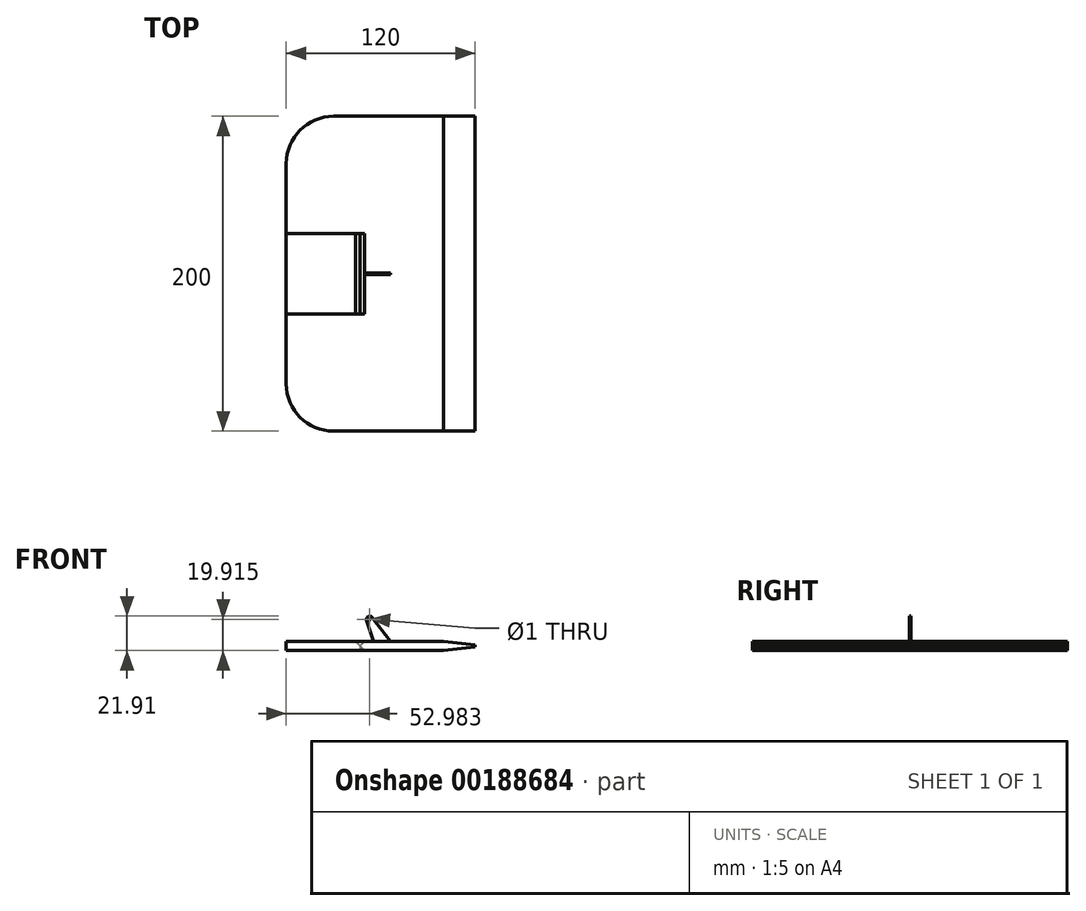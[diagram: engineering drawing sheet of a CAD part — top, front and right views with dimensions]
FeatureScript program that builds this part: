
annotation { "Feature Type Name" : "Feature", "Feature Type Description" : "" }
export const myFeature = defineFeature(function(context is Context, id is Id, definition is map)
    precondition{}
    {
        {
            var Q0;
            Q0=qCreatedBy(makeId("Top.planeOp"),FACE);
            var sketch = newSketch(context, id + "F0", { "sketchPlane" : qUnion([Q0])});
            skLineSegment(sketch, "E0.bottom", {"start": v(61.57, 100) * mm, "end": v(-28.43, 100) * mm});
            skLineSegment(sketch, "E0.top", {"start": v(61.57, -100) * mm, "end": v(-28.43, -100) * mm});
            skLineSegment(sketch, "E0.left", {"start": v(61.57, 100) * mm, "end": v(61.57, -100) * mm});
            skLineSegment(sketch, "E0.right", {"start": v(-58.43, 70) * mm, "end": v(-58.43, -70) * mm});
            skPoint(sketch, "E0.middle", {"position": v(1.57, 0) * mm});
            skPoint(sketch, "E1.visualSharp", {"position": v(-58.43, -100) * mm});
            skArc(sketch, "E1.filletArc", {"start": v(-58.43, -70) * mm, "mid": v(-49.64, -91.21) * mm, "end": v(-28.43, -100) * mm});
            skPoint(sketch, "E2.visualSharp", {"position": v(-58.43, 100) * mm});
            skArc(sketch, "E2.filletArc", {"start": v(-28.43, 100) * mm, "mid": v(-49.64, 91.21) * mm, "end": v(-58.43, 70) * mm});
            skLineSegment(sketch, "E3.bottom", {"start": v(-58.43, -25.5) * mm, "end": v(-11.6, -25.5) * mm});
            skLineSegment(sketch, "E3.left", {"start": v(-58.43, -25.5) * mm, "end": v(-58.43, 0) * mm});
            skLineSegment(sketch, "E3.right", {"start": v(-11.6, -25.5) * mm, "end": v(-11.6, 0) * mm});
            skLineSegment(sketch, "E4.MirrorCS", {"start": v(-58.43, 25.5) * mm, "end": v(-11.6, 25.5) * mm});
            skLineSegment(sketch, "E5.MirrorCS", {"start": v(-11.6, 25.5) * mm, "end": v(-11.6, 0) * mm});
            skLineSegment(sketch, "E6.MirrorCS", {"start": v(-58.43, 25.5) * mm, "end": v(-58.43, 0) * mm});
            skSolve(sketch);
        }
        {
            var Q0;
            Q0=makeQuery(id+"F0.imprint","IMPRINT",FACE,{"disambiguationData":[TD([[makeQuery(id+"F0.imprint","IMPRINT",EDGE,{"derivedFrom":sQuery(id+"F0.wireOp",EDGE,"E0.bottom")}),1.0]])]});
            extrude(context, id + "F1", {"entities" : qUnion([Q0]), "depth" : 6 * mm});
        }
        {
            var Q0;
            Q0=makeQuery(id+"F1.opExtrude","CAP_EDGE",EDGE,{"disambiguationData":[OSD([sQuery(id+"F0.wireOp",EDGE,"E0.left")])],"isStart":false});
            var Q1;
            Q1=makeQuery(id+"F1.opExtrude","CAP_EDGE",EDGE,{"disambiguationData":[OSD([sQuery(id+"F0.wireOp",EDGE,"E0.left")])],"isStart":true});
            chamfer(context, id + "F2", {"entities" : qUnion([Q0, Q1]), "chamferType" : ChamferType.TWO_OFFSETS, "width1" : 2.5 * mm, "oppositeDirection" : false, "width2" : 20 * mm, "tangentPropagation" : true});
        }
        {
            var Q0;
            Q0=makeQuery(id+"F0.imprint","IMPRINT",FACE,{"disambiguationData":[TD([[makeQuery(id+"F0.imprint","IMPRINT",EDGE,{"derivedFrom":sQuery(id+"F0.wireOp",EDGE,"E3.bottom")}),1.0]])]});
            var Q1;
            Q1=makeQuery(id+"F1.opExtrude","SWEPT_BODY",BODY,{"disambiguationData":[OSD([sQuery(id+"F0.wireOp",EDGE,"E0.bottom"),sQuery(id+"F0.wireOp",EDGE,"E0.top"),sQuery(id+"F0.wireOp",EDGE,"E0.left"),sQuery(id+"F0.wireOp",EDGE,"E0.right"),sQuery(id+"F0.wireOp",EDGE,"E1.filletArc"),sQuery(id+"F0.wireOp",EDGE,"E2.filletArc"),sQuery(id+"F0.wireOp",EDGE,"E3.bottom"),sQuery(id+"F0.wireOp",EDGE,"E3.right"),sQuery(id+"F0.wireOp",EDGE,"E4.MirrorCS"),sQuery(id+"F0.wireOp",EDGE,"E5.MirrorCS")])]});
            extrude(context, id + "F3", {"entities" : qUnion([Q0]), "endBoundEntityBody" : qUnion([Q1]), "depth" : 6 * mm});
        }
        {
            var Q0;
            Q0=makeQuery(id+"F1.opExtrude","CAP_EDGE",EDGE,{"disambiguationData":[OSD([sQuery(id+"F0.wireOp",EDGE,"E3.right"),sQuery(id+"F0.wireOp",EDGE,"E5.MirrorCS")])],"isStart":false});
            chamfer(context, id + "F4", {"entities" : qUnion([Q0]), "chamferType" : ChamferType.OFFSET_ANGLE, "width" : 3 * mm, "oppositeDirection" : false, "angle" : 45 * degree, "tangentPropagation" : true});
        }
        {
            var Q0;
            Q0=makeQuery(id+"F3.opExtrude","CAP_EDGE",EDGE,{"disambiguationData":[OSD([sQuery(id+"F0.wireOp",EDGE,"E3.right"),sQuery(id+"F0.wireOp",EDGE,"E5.MirrorCS")])],"isStart":false});
            chamfer(context, id + "F5", {"entities" : qUnion([Q0]), "chamferType" : ChamferType.OFFSET_ANGLE, "width" : 3 * mm, "oppositeDirection" : false, "angle" : 45 * degree, "tangentPropagation" : true});
        }
        {
            var Q0;
            Q0=makeQuery(id+"F1.opExtrude","CAP_EDGE",EDGE,{"disambiguationData":[OSD([sQuery(id+"F0.wireOp",EDGE,"E3.right"),sQuery(id+"F0.wireOp",EDGE,"E5.MirrorCS")])],"isStart":true});
            chamfer(context, id + "F6", {"entities" : qUnion([Q0]), "chamferType" : ChamferType.OFFSET_ANGLE, "width" : 3 * mm, "oppositeDirection" : false, "angle" : 45 * degree, "tangentPropagation" : true});
        }
        {
            var Q0;
            Q0=qCreatedBy(makeId("Front.planeOp"),FACE);
            var sketch = newSketch(context, id + "F7", { "sketchPlane" : qUnion([Q0])});
            skLineSegment(sketch, "E7.0.1", {"start": v(-8.6, 6) * mm, "end": v(-58.43, 6) * mm});
            skLineSegment(sketch, "E7.0.3", {"start": v(-58.43, 6) * mm, "end": v(-28.43, 6) * mm});
            skLineSegment(sketch, "E7.0.4", {"start": v(-28.43, 6) * mm, "end": v(41.57, 6) * mm});
            skLineSegment(sketch, "E7.0.6", {"start": v(41.57, 6) * mm, "end": v(-28.43, 6) * mm});
            skLineSegment(sketch, "E7.0.7", {"start": v(-28.43, 6) * mm, "end": v(-58.43, 6) * mm});
            skLineSegment(sketch, "E7.0.9", {"start": v(-58.43, 6) * mm, "end": v(-8.6, 6) * mm});
            skLineSegment(sketch, "E8.0.0", {"start": v(-58.43, 6) * mm, "end": v(-14.6, 6) * mm});
            skLineSegment(sketch, "E8.0.2", {"start": v(-14.6, 6) * mm, "end": v(-58.43, 6) * mm});
            skLineSegment(sketch, "E9.0.0", {"start": v(-14.6, 6) * mm, "end": v(-11.6, 3) * mm});
            skLineSegment(sketch, "E9.0.2", {"start": v(-11.6, 3) * mm, "end": v(-14.6, 6) * mm});
            skLineSegment(sketch, "E10.0.0", {"start": v(-8.6, 6) * mm, "end": v(-11.6, 3) * mm});
            skLineSegment(sketch, "E10.0.2", {"start": v(-11.6, 3) * mm, "end": v(-8.6, 6) * mm});
            skLineSegment(sketch, "E11.0.1", {"start": v(-58.43, 0) * mm, "end": v(-58.43, 6) * mm});
            skLineSegment(sketch, "E11.0.3", {"start": v(-58.43, 6) * mm, "end": v(-58.43, 0) * mm});
            skLineSegment(sketch, "E12.0.0", {"start": v(41.57, 6) * mm, "end": v(61.57, 3.5) * mm});
            skLineSegment(sketch, "E12.0.2", {"start": v(61.57, 3.5) * mm, "end": v(41.57, 6) * mm});
            skLineSegment(sketch, "E13.0.1", {"start": v(61.57, 0) * mm, "end": v(-28.43, 0) * mm});
            skLineSegment(sketch, "E13.0.2", {"start": v(-28.43, 0) * mm, "end": v(-58.43, 0) * mm});
            skLineSegment(sketch, "E13.0.4", {"start": v(-58.43, 0) * mm, "end": v(-11.6, 0) * mm});
            skLineSegment(sketch, "E13.0.7", {"start": v(-11.6, 0) * mm, "end": v(-58.43, 0) * mm});
            skLineSegment(sketch, "E13.0.9", {"start": v(-58.43, 0) * mm, "end": v(-28.43, 0) * mm});
            skLineSegment(sketch, "E13.0.10", {"start": v(-28.43, 0) * mm, "end": v(61.57, 0) * mm});
            skLineSegment(sketch, "E14.0.0", {"start": v(41.57, 0) * mm, "end": v(61.57, 2.5) * mm});
            skLineSegment(sketch, "E14.0.2", {"start": v(61.57, 2.5) * mm, "end": v(41.57, 0) * mm});
            skPoint(sketch, "E15.0", {"position": v(-11.6, 3) * mm});
            skPoint(sketch, "E16.0", {"position": v(-10.1, 1.5) * mm});
            skLineSegment(sketch, "E17.0", {"start": v(-8.6, 0) * mm, "end": v(-11.6, 3) * mm});
            skLineSegment(sketch, "E18.0", {"start": v(-11.6, 3) * mm, "end": v(-11.6, 0) * mm});
            skCircle(sketch, "E19", {"center": v(-11.6, 3) * mm, "radius": 18 * mm, "construction": true});
            skLineSegment(sketch, "E20", {"start": v(-11.6, 3) * mm, "end": v(6.4, 3) * mm, "construction": true});
            skLineSegment(sketch, "E21", {"start": v(-11.6, 3) * mm, "end": v(-5.45, 19.91) * mm, "construction": true});
            skCircle(sketch, "E22", {"center": v(-5.45, 19.91) * mm, "radius": 0.5 * mm});
            skCircle(sketch, "E23", {"center": v(-5.45, 19.91) * mm, "radius": 2 * mm});
            skLineSegment(sketch, "E24", {"start": v(-3.87, 21.14) * mm, "end": v(7.89, 6) * mm});
            skLineSegment(sketch, "E25", {"start": v(-7.35, 19.3) * mm, "end": v(-3, 6) * mm});
            skSolve(sketch);
        }
        {
            var Q0;
            {var subQ0=sQuery(id+"F7.wireOp",EDGE,"E24");Q0=makeQuery(id+"F7.imprint","IMPRINT",FACE,{"disambiguationData":[TD([[makeQuery(id+"F7.imprint","IMPRINT",EDGE,{"derivedFrom":subQ0}),-1.0]])]});}
            var Q1;
            Q1=makeQuery(id+"F7.imprint","IMPRINT",FACE,{"disambiguationData":[TD([[makeQuery(id+"F7.imprint","IMPRINT",EDGE,{"derivedFrom":sQuery(id+"F7.wireOp",EDGE,"E22")}),-1.0]])]});
            extrude(context, id + "F8", {"entities" : qUnion([Q0, Q1]), "operationType" : NewBodyOperationType.ADD, "depth" : 1 * mm, "symmetric" : true});
        }
    });
